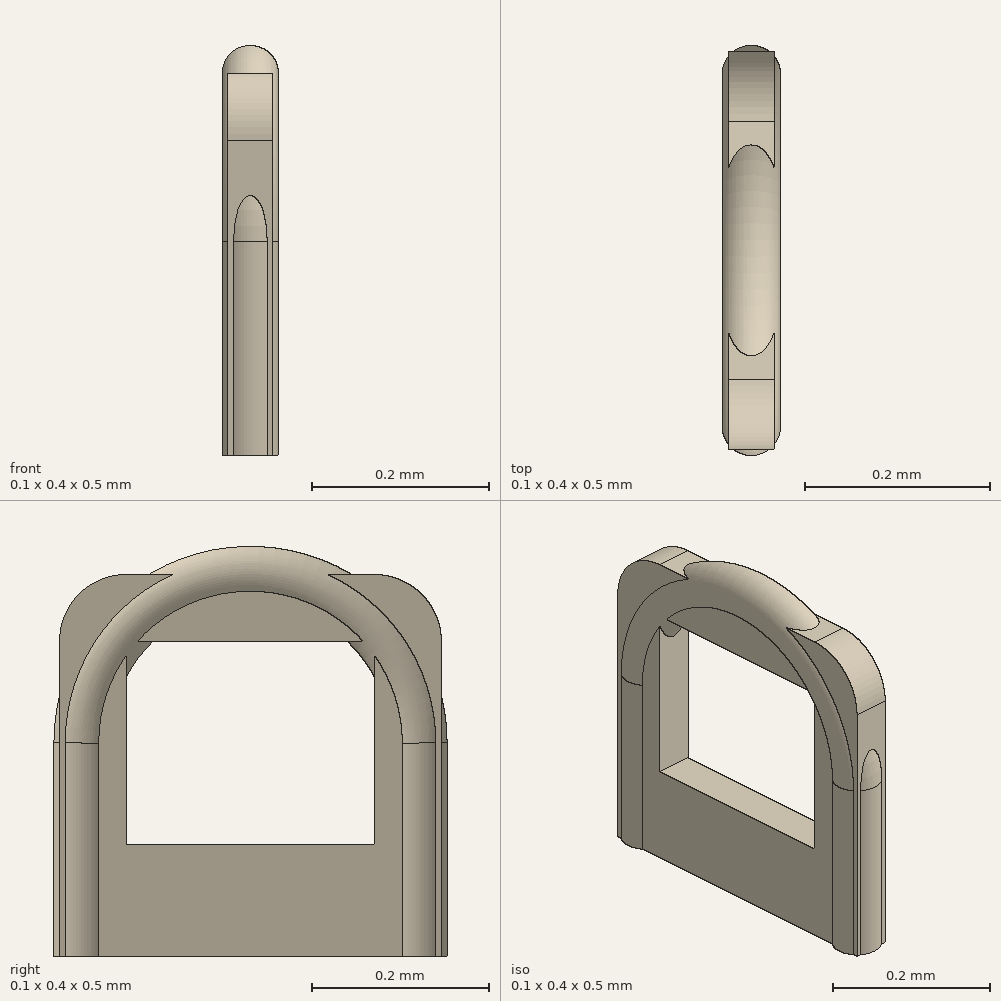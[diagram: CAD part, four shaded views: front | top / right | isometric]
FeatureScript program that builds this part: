
annotation { "Feature Type Name" : "Feature", "Feature Type Description" : "" }
export const myFeature = defineFeature(function(context is Context, id is Id, definition is map)
    precondition{}
    {
        {
            var Q0;
            Q0=qCreatedBy(makeId("Right.planeOp"),FACE);
            var sketch = newSketch(context, id + "F0", { "sketchPlane" : qUnion([Q0])});
            skLineSegment(sketch, "E0", {"start": v(-0.2, 0) * mm, "end": v(-0.2, 0.24) * mm});
            skLineSegment(sketch, "E1", {"start": v(0, 0) * mm, "end": v(0, 0.43) * mm, "construction": true});
            skLineSegment(sketch, "E2.MirrorCS", {"start": v(0.2, 0) * mm, "end": v(0.2, 0.24) * mm});
            skArc(sketch, "E3", {"start": v(-0.2, 0.24) * mm, "mid": v(0, 0.43) * mm, "end": v(0.2, 0.24) * mm});
            skSolve(sketch);
        }
        {
            var Q0;
            Q0=qCreatedBy(makeId("Top.planeOp"),FACE);
            var sketch = newSketch(context, id + "F1", { "sketchPlane" : qUnion([Q0])});
            skCircle(sketch, "E4", {"center": v(0, -0.2) * mm, "radius": 0.03 * mm});
            skSolve(sketch);
        }
        {
            var Q0;
            Q0=makeQuery(id+"F1.imprint","IMPRINT",FACE,{"disambiguationData":[TD([[makeQuery(id+"F1.imprint","IMPRINT",EDGE,{"derivedFrom":sQuery(id+"F1.wireOp",EDGE,"E4")}),1.0]])]});
            var Q1;
            Q1=sQuery(id+"F0.wireOp",EDGE,"E0");
            var Q2;
            Q2=sQuery(id+"F0.wireOp",EDGE,"E3");
            var Q3;
            Q3=sQuery(id+"F0.wireOp",EDGE,"E2.MirrorCS");
            sweep(context, id + "F2", {"profiles" : qUnion([Q0]), "path" : qUnion([Q1, Q2, Q3])});
        }
        {
            var Q0;
            Q0=qCreatedBy(makeId("Right.planeOp"),FACE);
            var sketch = newSketch(context, id + "F3", { "sketchPlane" : qUnion([Q0])});
            skLineSegment(sketch, "E5", {"start": v(-0.22, 0) * mm, "end": v(0.22, 0) * mm});
            skLineSegment(sketch, "E6", {"start": v(-0.14, 0.43) * mm, "end": v(0.14, 0.43) * mm});
            skPoint(sketch, "E7", {"position": v(0, 0.43) * mm});
            skLineSegment(sketch, "E8", {"start": v(-0.22, 0) * mm, "end": v(-0.22, 0.36) * mm});
            skArc(sketch, "E9", {"start": v(-0.14, 0.43) * mm, "mid": v(-0.2, 0.4) * mm, "end": v(-0.22, 0.36) * mm});
            skLineSegment(sketch, "E10", {"start": v(0, 0) * mm, "end": v(0, 0.43) * mm, "construction": true});
            skArc(sketch, "E11.MirrorCS", {"start": v(0.14, 0.43) * mm, "mid": v(0.2, 0.4) * mm, "end": v(0.22, 0.36) * mm});
            skLineSegment(sketch, "E12.MirrorCS", {"start": v(0.22, 0) * mm, "end": v(0.22, 0.36) * mm});
            skLineSegment(sketch, "E13", {"start": v(-0.14, 0.36) * mm, "end": v(0.14, 0.36) * mm});
            skLineSegment(sketch, "E14", {"start": v(0.14, 0.36) * mm, "end": v(0.14, 0.13) * mm});
            skLineSegment(sketch, "E15", {"start": v(0.14, 0.13) * mm, "end": v(-0.14, 0.13) * mm});
            skLineSegment(sketch, "E16", {"start": v(-0.14, 0.13) * mm, "end": v(-0.14, 0.36) * mm});
            skSolve(sketch);
        }
        {
            var Q0;
            Q0=makeQuery(id+"F3.imprint","IMPRINT",FACE,{"disambiguationData":[TD([[makeQuery(id+"F3.imprint","IMPRINT",EDGE,{"derivedFrom":sQuery(id+"F3.wireOp",EDGE,"E5")}),1.0]])]});
            extrude(context, id + "F4", {"entities" : qUnion([Q0]), "depth" : 0.05 * mm, "symmetric" : true});
        }
    });
